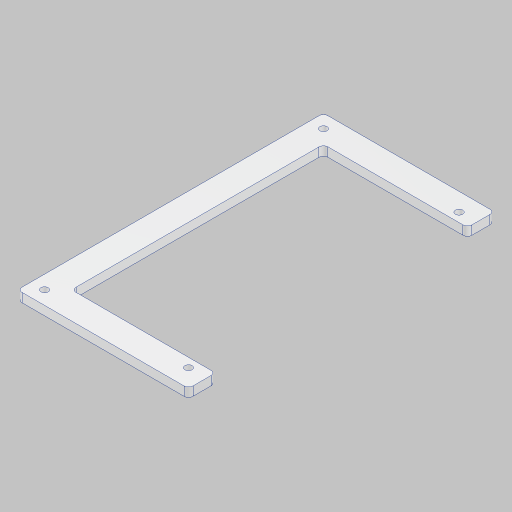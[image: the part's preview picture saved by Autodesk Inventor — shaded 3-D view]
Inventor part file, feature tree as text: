
AUTODESK INVENTOR PART (.ipt)
format: ipt  version: 2023.5 (Build 275446000, 446)  size: 292,352 bytes
history: native  units: in
note: dims shown in document units (in); Inventor stores cm internally (conversion verified against a paired STEP export)
features: hole x3, sketch x1, extrude x1, fillet x1
ambient origin geometry x8: Origin, YZ Plane, XZ Plane, XY Plane, X Axis, Y Axis, Z Axis, Center Point
bodies: Solid1 (feature_tree)
feature tree (6):
  sketch  "Sketch1"  dims[d0=3.0in d1=0.75in d3=0.75in d4=3.0in d5=0.75in d6=0.25in d7=0.0in d8=7.0in d9=1.0in d10=0.75in d11=1.0in d12=0.75in d17=0.2in d18=0.25in d20=0.2in d21=0.5in d22=0.5in d23=0.5in d24=0.201in d25=0.75in d26=0.375in d27=0.25in d28=0.5635in d29=1.0in d30=0.8108in d31=0.201in d32=0.75in d33=0.375in d34=0.25in d35=0.5635in d36=1.0in d37=0.8108in d38=0.2in d39=0.375in d40=0.375in d41=0.2in d42=0.375in d43=0.375in d44=0.201in d45=0.75in d46=0.375in d47=0.25in d48=0.5635in d49=1.0in d50=0.8108in d51=0.125in]
  extrude  "Extrusion1"  Depth=0.75in
  hole  "Hole1"  [1 undecoded]
  hole  "Hole2"  [1 undecoded]
  hole  "Hole3"  [1 undecoded]
  fillet  "Fillet1"  Radius=0.25in
note: 3 required parameter values undecoded (feature->parameter linkage not recoverable at this tier; creation-order binding heuristic only, values carry confidence <= 0.55)
